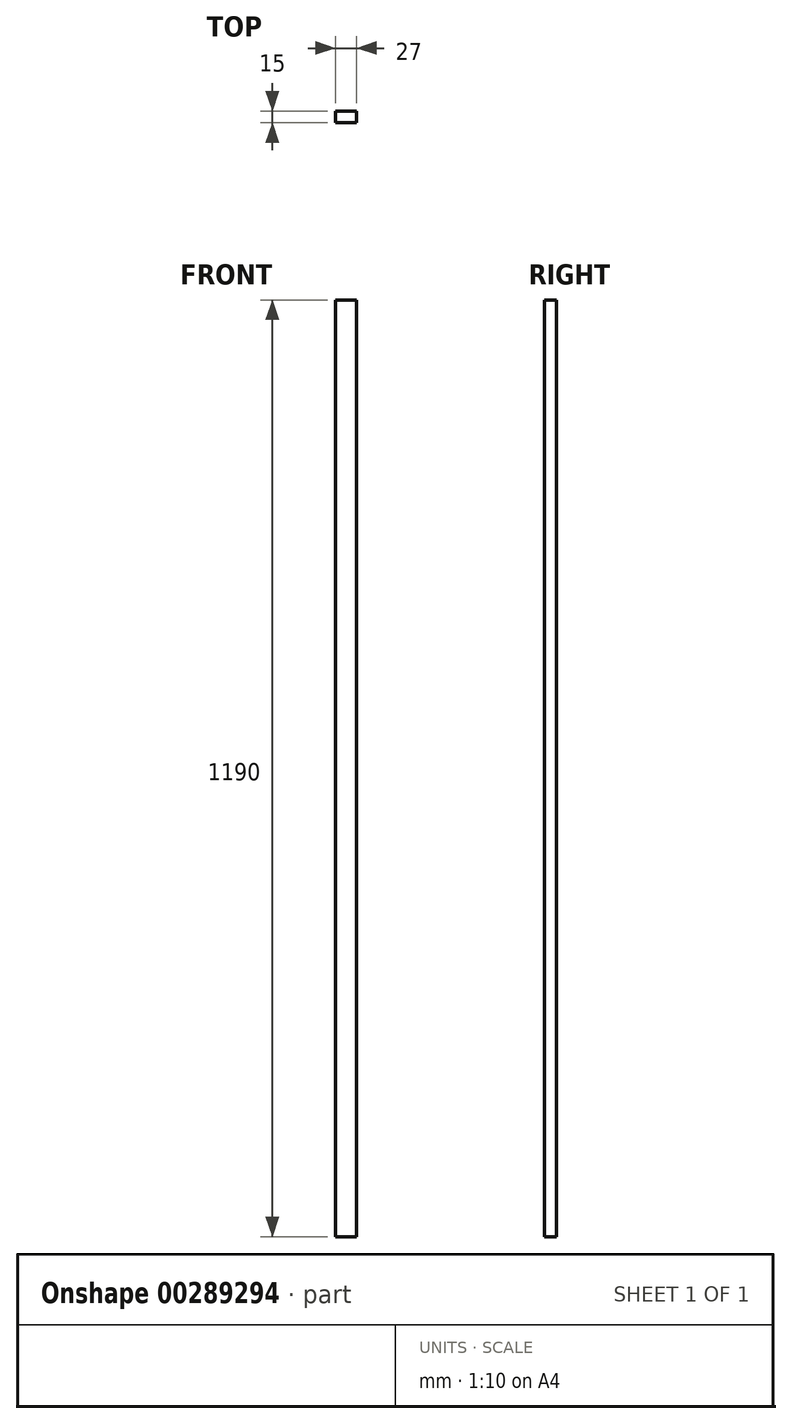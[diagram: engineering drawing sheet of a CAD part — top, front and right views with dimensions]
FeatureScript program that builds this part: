
annotation { "Feature Type Name" : "Feature", "Feature Type Description" : "" }
export const myFeature = defineFeature(function(context is Context, id is Id, definition is map)
    precondition{}
    {
        {
            var Q0;
            Q0=qCreatedBy(makeId("Top.planeOp"),FACE);
            var sketch = newSketch(context, id + "F0", { "sketchPlane" : qUnion([Q0])});
            skLineSegment(sketch, "E0.bottom", {"start": v(0, 0) * mm, "end": v(27, 0) * mm});
            skLineSegment(sketch, "E0.top", {"start": v(0, -15) * mm, "end": v(27, -15) * mm});
            skLineSegment(sketch, "E0.left", {"start": v(0, 0) * mm, "end": v(0, -15) * mm});
            skLineSegment(sketch, "E0.right", {"start": v(27, 0) * mm, "end": v(27, -15) * mm});
            skSolve(sketch);
        }
        {
            var Q0;
            Q0=makeQuery(id+"F0.imprint","IMPRINT",FACE,{"disambiguationData":[TD([[makeQuery(id+"F0.imprint","IMPRINT",EDGE,{"derivedFrom":sQuery(id+"F0.wireOp",EDGE,"E0.bottom")}),-1.0]])]});
            extrude(context, id + "F1", {"entities" : qUnion([Q0]), "depth" : 1190 * mm});
        }
    });
